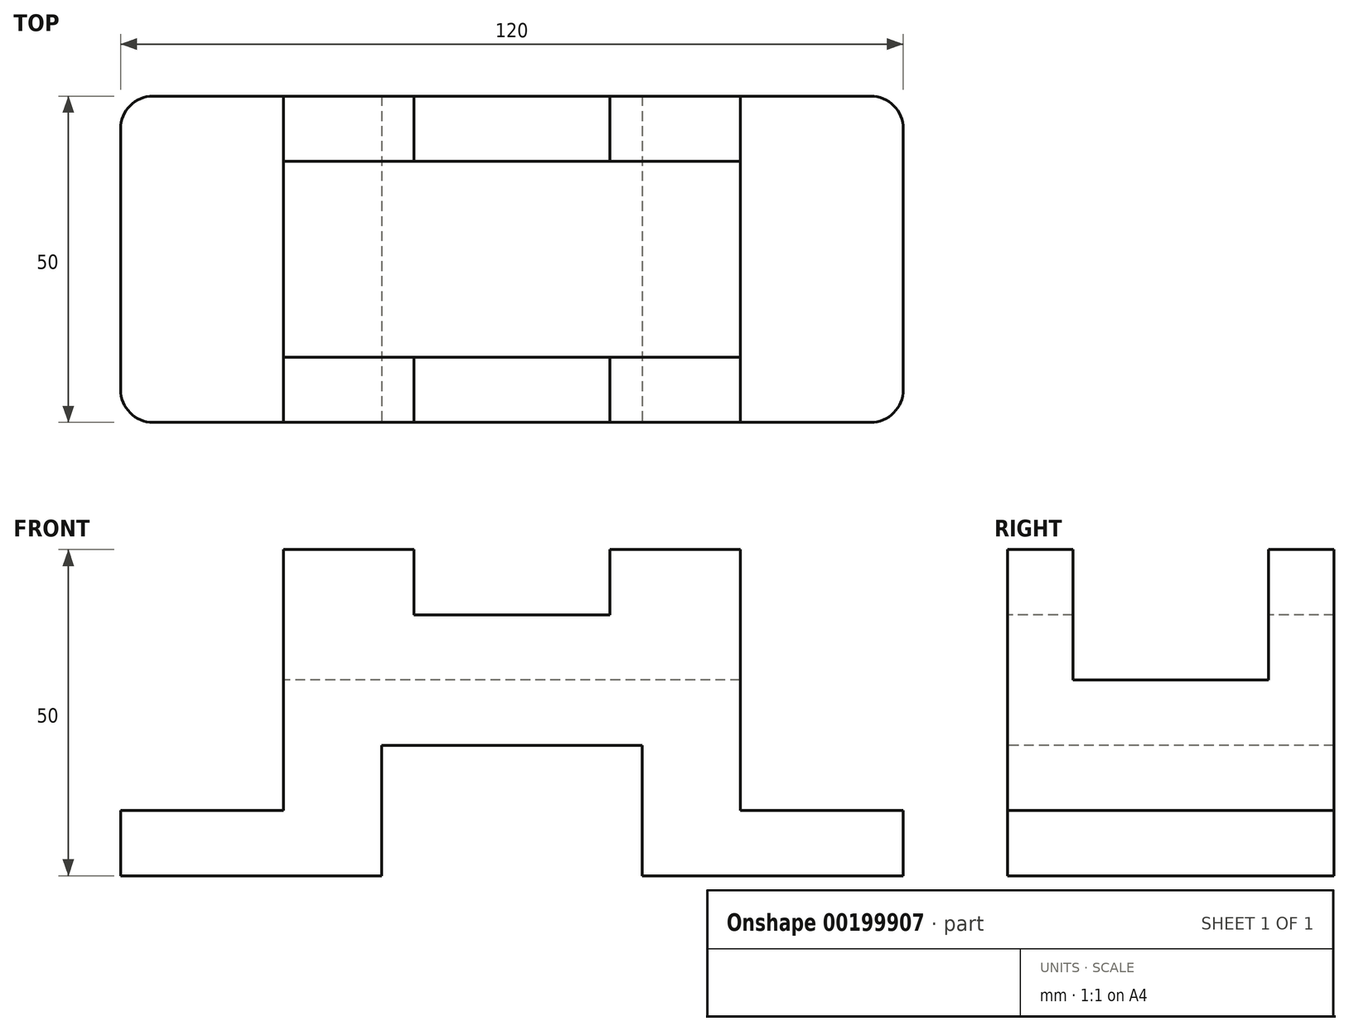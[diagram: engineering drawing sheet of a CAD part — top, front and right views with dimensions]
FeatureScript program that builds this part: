
annotation { "Feature Type Name" : "Feature", "Feature Type Description" : "" }
export const myFeature = defineFeature(function(context is Context, id is Id, definition is map)
    precondition{}
    {
        {
            var Q0;
            Q0=qCreatedBy(makeId("Right.planeOp"),FACE);
            var sketch = newSketch(context, id + "F0", { "sketchPlane" : qUnion([Q0])});
            skLineSegment(sketch, "E0", {"start": v(0, 0) * mm, "end": v(25, 0) * mm});
            skLineSegment(sketch, "E1", {"start": v(25, 0) * mm, "end": v(25, 50) * mm});
            skLineSegment(sketch, "E2", {"start": v(25, 50) * mm, "end": v(15, 50) * mm});
            skLineSegment(sketch, "E3", {"start": v(15, 50) * mm, "end": v(15, 30) * mm});
            skLineSegment(sketch, "E4", {"start": v(15, 30) * mm, "end": v(0, 30) * mm});
            skLineSegment(sketch, "E5", {"start": v(0, 30) * mm, "end": v(0, 0) * mm});
            skLineSegment(sketch, "E6", {"start": v(0, 10) * mm, "end": v(25, 10) * mm});
            skSolve(sketch);
        }
        {
            var Q0;
            {var subQ0=sQuery(id+"F0.wireOp",EDGE,"E0");Q0=makeQuery(id+"F0.imprint","IMPRINT",FACE,{"disambiguationData":[TD([[makeQuery(id+"F0.imprint","IMPRINT",EDGE,{"derivedFrom":subQ0}),1.0]])]});}
            extrude(context, id + "F1", {"entities" : qUnion([Q0]), "depth" : 60 * mm});
        }
        {
            var Q0;
            Q0=makeQuery(id+"F1.opExtrude","CAP_EDGE",EDGE,{"disambiguationData":[OSD([sQuery(id+"F0.wireOp",EDGE,"E1")])],"isStart":false});
            fillet(context, id + "F2", {"entities" : qUnion([Q0]), "radius" : 5 * mm, "tangentPropagation" : true, "allowEdgeOverflow" : false});
        }
        {
            var Q0;
            {var subQ1=sQuery(id+"F0.wireOp",EDGE,"E2");Q0=makeQuery(id+"F0.imprint","IMPRINT",FACE,{"disambiguationData":[TD([[makeQuery(id+"F0.imprint","IMPRINT",EDGE,{"derivedFrom":subQ1}),1.0]])]});}
            extrude(context, id + "F3", {"entities" : qUnion([Q0]), "operationType" : NewBodyOperationType.ADD, "depth" : 35 * mm});
        }
        {
            var Q0;
            Q0=makeQuery(id+"F1.opExtrude","SWEPT_BODY",BODY,{"disambiguationData":[OSD([sQuery(id+"F0.wireOp",EDGE,"E0"),sQuery(id+"F0.wireOp",EDGE,"E1"),sQuery(id+"F0.wireOp",EDGE,"E5"),sQuery(id+"F0.wireOp",EDGE,"E6")])]});
            var Q1;
            Q1=qCreatedBy(makeId("Right.planeOp"),FACE);
            mirror(context, id + "F4", {"operationType" : NewBodyOperationType.ADD, "entities" : qUnion([Q0]), "mirrorPlane" : qUnion([Q1])});
        }
        {
            var Q0;
            Q0=makeQuery(id+"F1.opExtrude","SWEPT_BODY",BODY,{"disambiguationData":[OSD([sQuery(id+"F0.wireOp",EDGE,"E0"),sQuery(id+"F0.wireOp",EDGE,"E1"),sQuery(id+"F0.wireOp",EDGE,"E5"),sQuery(id+"F0.wireOp",EDGE,"E6")])]});
            var Q1;
            Q1=qCreatedBy(makeId("Front.planeOp"),FACE);
            mirror(context, id + "F5", {"operationType" : NewBodyOperationType.ADD, "entities" : qUnion([Q0]), "mirrorPlane" : qUnion([Q1])});
        }
        {
            var Q0;
            {var subQ0=sQuery(id+"F0.wireOp",EDGE,"E1");var subQ1=makeQuery(id+"F3.boolean.opBoolean","MERGE",FACE,{"derivedFrom":[makeQuery(id+"F1.opExtrude","SWEPT_FACE",FACE,{"disambiguationData":[OSD([subQ0])]}),makeQuery(id+"F3.opExtrude","SWEPT_FACE",FACE,{"disambiguationData":[OSD([subQ0])]})]});Q0=makeQuery(id+"F5.opPattern","COPY",FACE,{"derivedFrom":makeQuery(id+"F4.boolean.opBoolean","MERGE",FACE,{"derivedFrom":[subQ1,makeQuery(id+"F4.opPattern","COPY",FACE,{"derivedFrom":subQ1,"instanceName":"1"})]}),"instanceName":"1"});}
            var sketch = newSketch(context, id + "F6", { "sketchPlane" : qUnion([Q0])});
            skLineSegment(sketch, "E7", {"start": v(0, 0) * mm, "end": v(20, 0) * mm});
            skLineSegment(sketch, "E8", {"start": v(20, 0) * mm, "end": v(20, 20) * mm});
            skLineSegment(sketch, "E9", {"start": v(0, 0) * mm, "end": v(-20, 0) * mm});
            skLineSegment(sketch, "E10", {"start": v(-20, 0) * mm, "end": v(-20, 20) * mm});
            skLineSegment(sketch, "E11", {"start": v(-20, 20) * mm, "end": v(20, 20) * mm});
            skLineSegment(sketch, "E12", {"start": v(0, 50) * mm, "end": v(15, 50) * mm});
            skLineSegment(sketch, "E13", {"start": v(15, 50) * mm, "end": v(15, 40) * mm});
            skLineSegment(sketch, "E14", {"start": v(15, 40) * mm, "end": v(-15, 40) * mm});
            skLineSegment(sketch, "E15", {"start": v(-15, 40) * mm, "end": v(-15, 50) * mm});
            skLineSegment(sketch, "E16", {"start": v(-15, 50) * mm, "end": v(0, 50) * mm});
            skSolve(sketch);
        }
        {
            var Q0;
            Q0=makeQuery(id+"F6.imprint","IMPRINT",FACE,{"disambiguationData":[TD([[makeQuery(id+"F6.imprint","IMPRINT",EDGE,{"derivedFrom":sQuery(id+"F6.wireOp",EDGE,"E7")}),-1.0]])]});
            var Q1;
            Q1=makeQuery(id+"F6.imprint","IMPRINT",FACE,{"disambiguationData":[TD([[makeQuery(id+"F6.imprint","IMPRINT",EDGE,{"derivedFrom":sQuery(id+"F6.wireOp",EDGE,"E12")}),1.0]])]});
            extrude(context, id + "F7", {"entities" : qUnion([Q0, Q1]), "operationType" : NewBodyOperationType.REMOVE, "oppositeDirection" : true, "depth" : 50 * mm});
        }
    });
